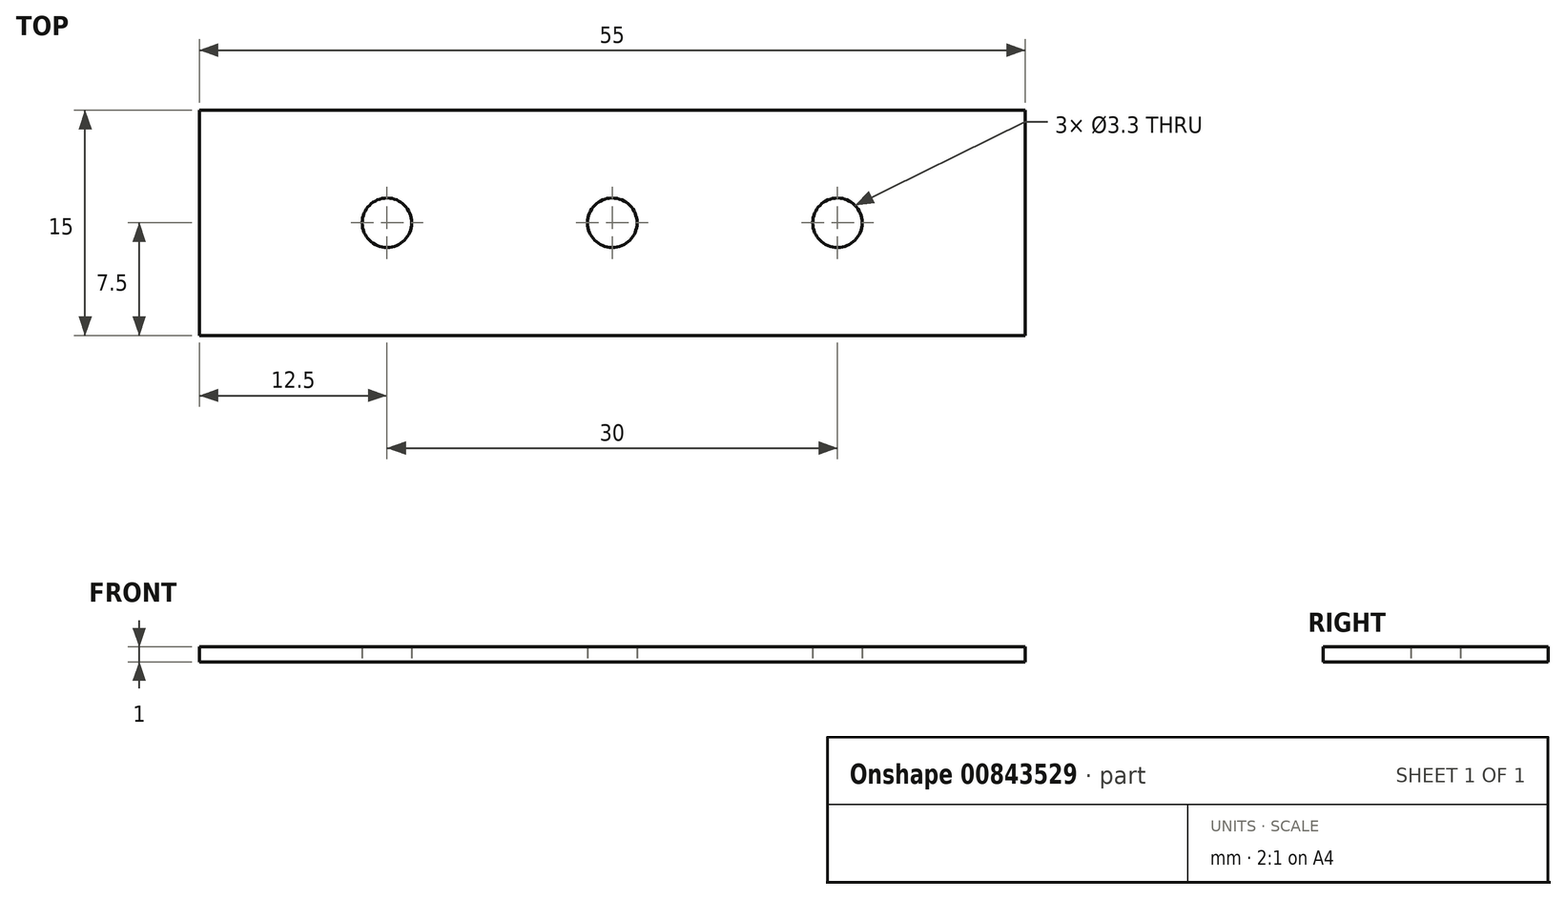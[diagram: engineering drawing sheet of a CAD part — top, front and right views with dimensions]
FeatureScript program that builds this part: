
annotation { "Feature Type Name" : "Feature", "Feature Type Description" : "" }
export const myFeature = defineFeature(function(context is Context, id is Id, definition is map)
    precondition{}
    {
        {
            var Q0;
            Q0=qCreatedBy(makeId("Top.planeOp"),FACE);
            var sketch = newSketch(context, id + "F0", { "sketchPlane" : qUnion([Q0])});
            skLineSegment(sketch, "E0.bottom", {"start": v(27.5, 7.5) * mm, "end": v(-27.5, 7.5) * mm});
            skLineSegment(sketch, "E0.top", {"start": v(27.5, -7.5) * mm, "end": v(-27.5, -7.5) * mm});
            skLineSegment(sketch, "E0.left", {"start": v(27.5, 7.5) * mm, "end": v(27.5, -7.5) * mm});
            skLineSegment(sketch, "E0.right", {"start": v(-27.5, 7.5) * mm, "end": v(-27.5, -7.5) * mm});
            skPoint(sketch, "E0.middle", {"position": v(0, 0) * mm});
            skCircle(sketch, "E1", {"center": v(-15, 0) * mm, "radius": 1.65 * mm});
            skCircle(sketch, "E2", {"center": v(0, 0) * mm, "radius": 1.65 * mm});
            skCircle(sketch, "E3", {"center": v(15, 0) * mm, "radius": 1.65 * mm});
            skSolve(sketch);
        }
        {
            var Q0;
            Q0 = qSketchRegion(id + "F0", true);
            extrude(context, id + "F1", {"entities" : qUnion([Q0]), "depth" : 1 * mm, "offsetDistance" : 25 * mm});
        }
    });
